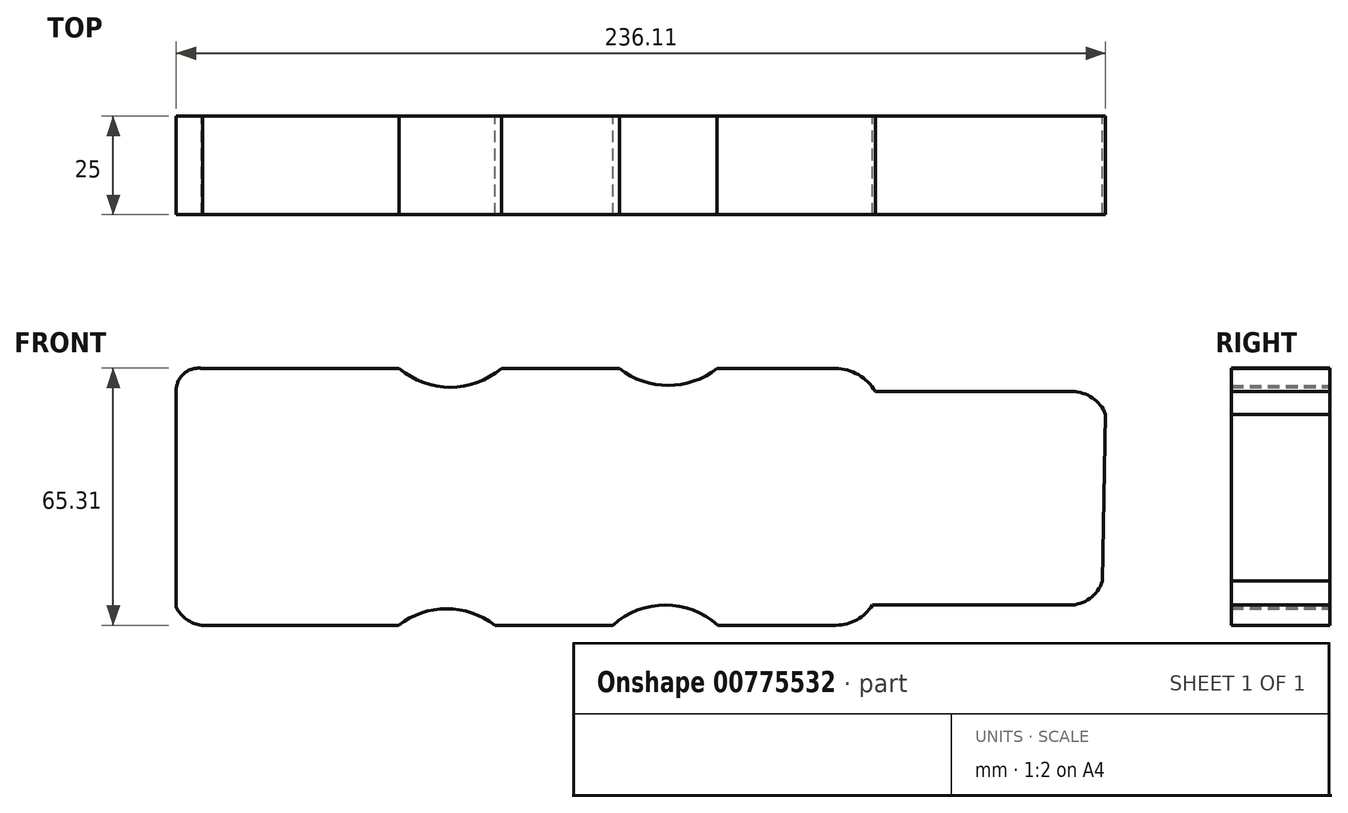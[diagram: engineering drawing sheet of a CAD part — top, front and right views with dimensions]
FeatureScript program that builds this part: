
annotation { "Feature Type Name" : "Feature", "Feature Type Description" : "" }
export const myFeature = defineFeature(function(context is Context, id is Id, definition is map)
    precondition{}
    {
        {
            var Q0;
            Q0=qCreatedBy(makeId("Front.planeOp"),FACE);
            var sketch = newSketch(context, id + "F0", { "sketchPlane" : qUnion([Q0])});
            skLineSegment(sketch, "E0", {"start": v(-99.1, 28.23) * mm, "end": v(-99.1, -26.77) * mm});
            skArc(sketch, "E1", {"start": v(-92.44, 33.85) * mm, "mid": v(-97.07, 32.58) * mm, "end": v(-99.1, 28.23) * mm});
            skLineSegment(sketch, "E2", {"start": v(-92.44, 33.85) * mm, "end": v(-42.44, 33.85) * mm});
            skArc(sketch, "E3", {"start": v(-99.1, -26.77) * mm, "mid": v(-96.46, -29.92) * mm, "end": v(-92.63, -31.38) * mm});
            skLineSegment(sketch, "E4", {"start": v(-92.63, -31.38) * mm, "end": v(-42.63, -31.38) * mm});
            skArc(sketch, "E5", {"start": v(-42.44, 33.85) * mm, "mid": v(-29.47, 29.08) * mm, "end": v(-16.5, 33.85) * mm});
            skArc(sketch, "E6", {"start": v(-18.16, -31.38) * mm, "mid": v(-30.4, -27.2) * mm, "end": v(-42.63, -31.38) * mm});
            skLineSegment(sketch, "E7", {"start": v(-16.5, 33.85) * mm, "end": v(13.5, 33.85) * mm});
            skLineSegment(sketch, "E8", {"start": v(-18.16, -31.38) * mm, "end": v(11.84, -31.38) * mm});
            skArc(sketch, "E9", {"start": v(13.5, 33.85) * mm, "mid": v(25.9, 29.54) * mm, "end": v(38.3, 33.85) * mm});
            skArc(sketch, "E10", {"start": v(38.54, -31.38) * mm, "mid": v(25.19, -26.28) * mm, "end": v(11.84, -31.38) * mm});
            skLineSegment(sketch, "E11", {"start": v(38.3, 33.85) * mm, "end": v(68.3, 33.85) * mm});
            skLineSegment(sketch, "E12", {"start": v(38.54, -31.38) * mm, "end": v(68.54, -31.38) * mm});
            skArc(sketch, "E13", {"start": v(78.51, 27.97) * mm, "mid": v(74.2, 32.28) * mm, "end": v(68.3, 33.85) * mm});
            skLineSegment(sketch, "E14", {"start": v(78.51, 27.97) * mm, "end": v(128.51, 27.97) * mm});
            skArc(sketch, "E15", {"start": v(68.54, -31.38) * mm, "mid": v(73.81, -30.02) * mm, "end": v(77.78, -26.28) * mm});
            skPoint(sketch, "E15.endSnap0", {"position": v(25.19, -26.28) * mm});
            skLineSegment(sketch, "E16", {"start": v(77.78, -26.28) * mm, "end": v(127.78, -26.28) * mm});
            skArc(sketch, "E17", {"start": v(137.02, 22.2) * mm, "mid": v(133.65, 26.4) * mm, "end": v(128.51, 27.97) * mm});
            skArc(sketch, "E18", {"start": v(127.78, -26.28) * mm, "mid": v(133, -24.59) * mm, "end": v(136.25, -20.15) * mm});
            skLineSegment(sketch, "E19", {"start": v(137.02, 22.2) * mm, "end": v(136.25, -20.15) * mm});
            skSolve(sketch);
        }
        {
            var Q0;
            Q0 = qSketchRegion(id + "F0", true);
            extrude(context, id + "F1", {"entities" : qUnion([Q0]), "depth" : 25 * mm, "offsetDistance" : 25 * mm});
        }
    });
